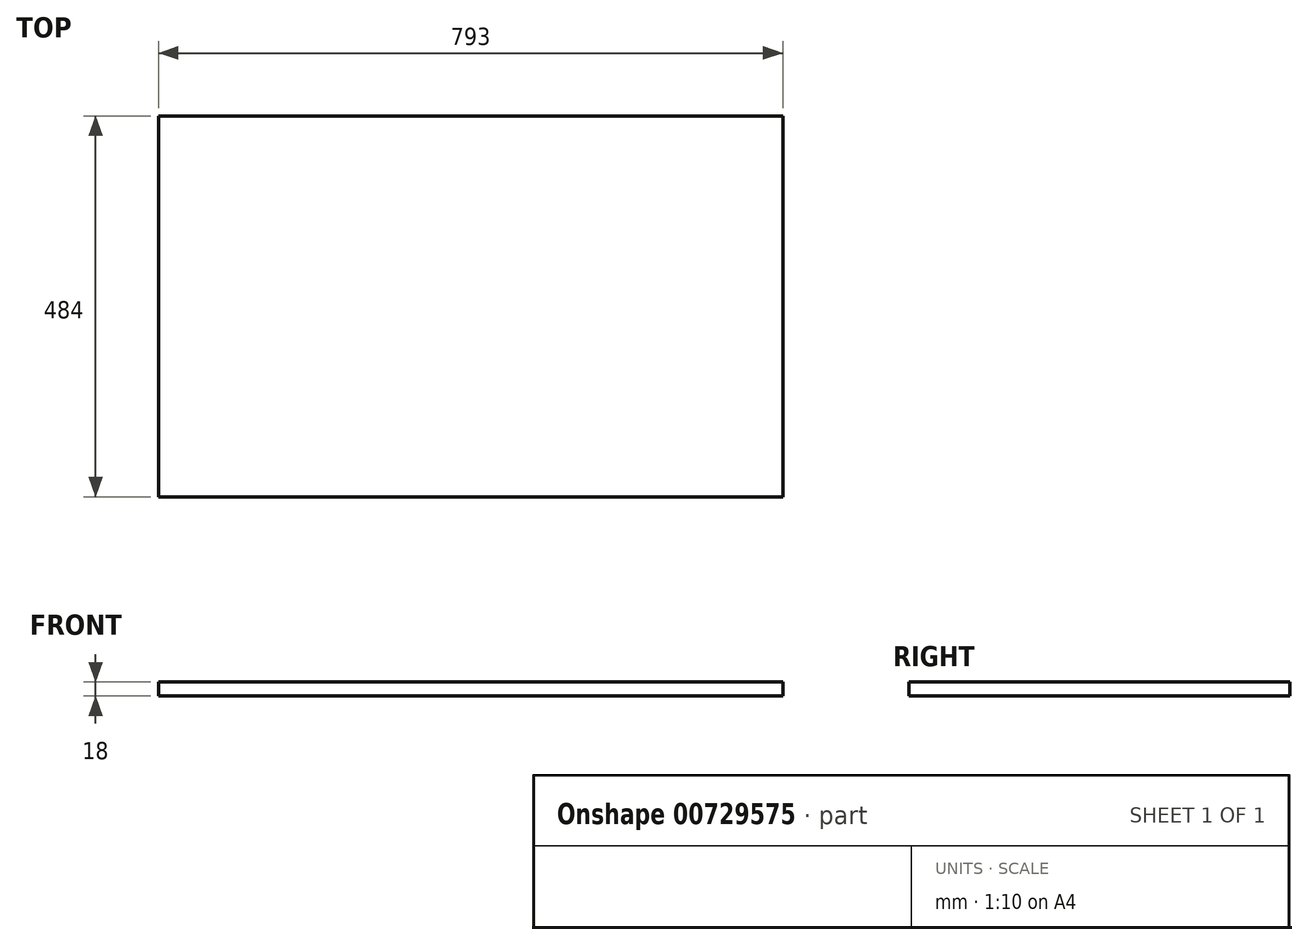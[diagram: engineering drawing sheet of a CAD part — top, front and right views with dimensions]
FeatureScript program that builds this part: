
annotation { "Feature Type Name" : "Feature", "Feature Type Description" : "" }
export const myFeature = defineFeature(function(context is Context, id is Id, definition is map)
    precondition{}
    {
        {
            var Q0;
            Q0=qCreatedBy(makeId("Top.planeOp"),FACE);
            var sketch = newSketch(context, id + "F0", { "sketchPlane" : qUnion([Q0])});
            skLineSegment(sketch, "E0.bottom", {"start": v(396.5, -242) * mm, "end": v(-396.5, -242) * mm});
            skLineSegment(sketch, "E0.top", {"start": v(396.5, 242) * mm, "end": v(-396.5, 242) * mm});
            skLineSegment(sketch, "E0.left", {"start": v(396.5, -242) * mm, "end": v(396.5, 242) * mm});
            skLineSegment(sketch, "E0.right", {"start": v(-396.5, -242) * mm, "end": v(-396.5, 242) * mm});
            skPoint(sketch, "E0.middle", {"position": v(0, 0) * mm});
            skSolve(sketch);
        }
        {
            var Q0;
            Q0=makeQuery(id+"F0.imprint","IMPRINT",FACE,{"disambiguationData":[TD([[makeQuery(id+"F0.imprint","IMPRINT",EDGE,{"derivedFrom":sQuery(id+"F0.wireOp",EDGE,"E0.bottom")}),-1.0]])]});
            extrude(context, id + "F1", {"entities" : qUnion([Q0]), "depth" : 18 * mm, "offsetDistance" : 25 * mm});
        }
    });
